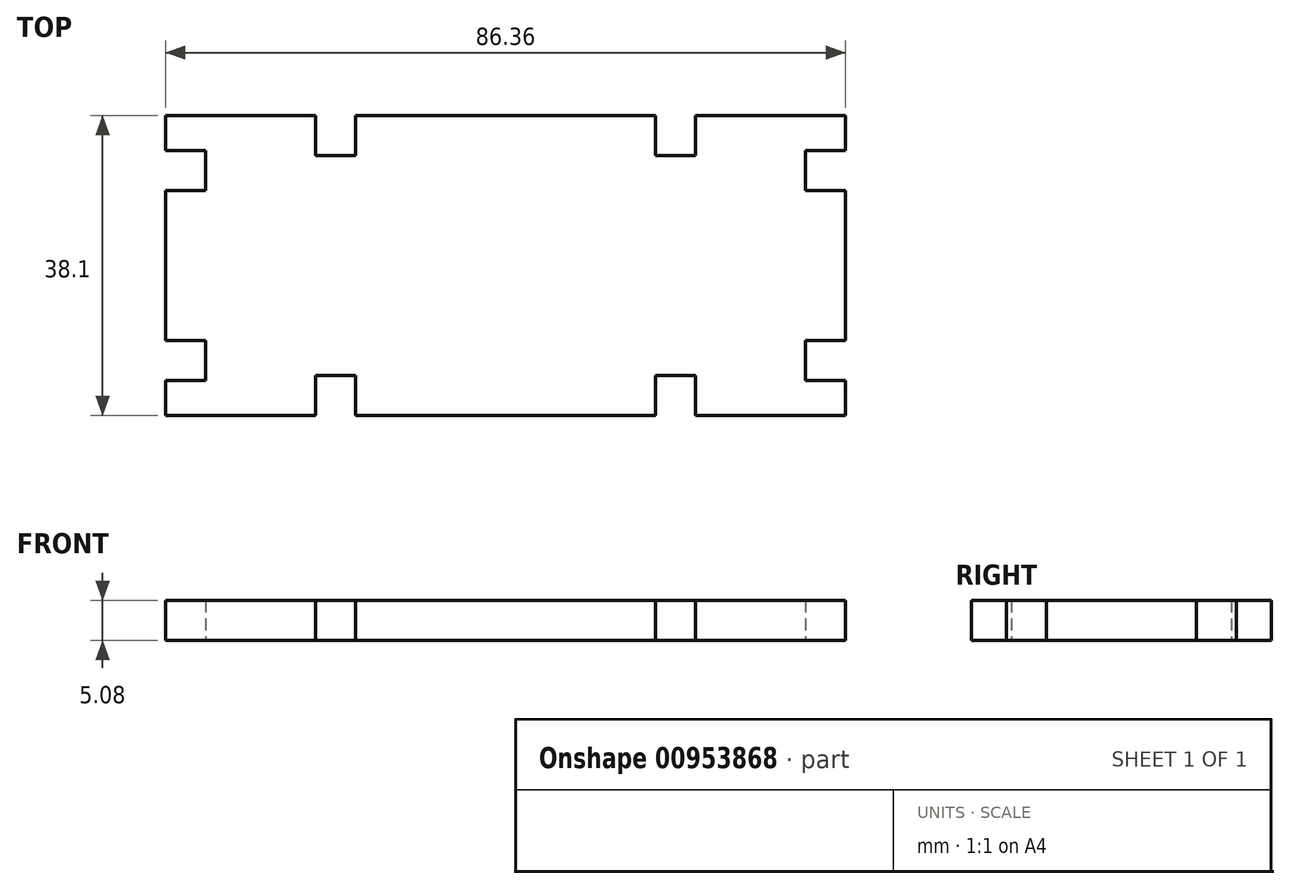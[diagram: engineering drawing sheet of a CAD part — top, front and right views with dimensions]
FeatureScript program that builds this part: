
annotation { "Feature Type Name" : "Feature", "Feature Type Description" : "" }
export const myFeature = defineFeature(function(context is Context, id is Id, definition is map)
    precondition{}
    {
        {
            var Q0;
            Q0=qCreatedBy(makeId("Top.planeOp"),FACE);
            var sketch = newSketch(context, id + "F0", { "sketchPlane" : qUnion([Q0])});
            skLineSegment(sketch, "E0.top", {"start": v(-43.18, -19.05) * mm, "end": v(43.18, -19.05) * mm});
            skLineSegment(sketch, "E0.right", {"start": v(43.18, 19.05) * mm, "end": v(43.18, -19.05) * mm});
            skPoint(sketch, "E0.middle", {"position": v(0, 0) * mm});
            skLineSegment(sketch, "E1", {"start": v(-43.18, 0) * mm, "end": v(43.18, 0) * mm});
            skLineSegment(sketch, "E2", {"start": v(-43.18, 19.05) * mm, "end": v(-43.18, 0) * mm});
            skLineSegment(sketch, "E3", {"start": v(-43.18, 0) * mm, "end": v(-43.18, -19.05) * mm});
            skLineSegment(sketch, "E4", {"start": v(0, 0) * mm, "end": v(0, 19.05) * mm});
            skLineSegment(sketch, "E5", {"start": v(-43.18, 19.05) * mm, "end": v(0, 19.05) * mm});
            skLineSegment(sketch, "E6", {"start": v(0, 19.05) * mm, "end": v(43.18, 19.05) * mm});
            skLineSegment(sketch, "E7", {"start": v(0, 19.05) * mm, "end": v(-38.1, 19.05) * mm});
            skLineSegment(sketch, "E8", {"start": v(0, 19.05) * mm, "end": v(38.1, 19.05) * mm});
            skLineSegment(sketch, "E9", {"start": v(-19.05, 19.05) * mm, "end": v(-19.05, 13.97) * mm});
            skLineSegment(sketch, "E10", {"start": v(-19.05, 13.97) * mm, "end": v(-24.13, 13.97) * mm});
            skLineSegment(sketch, "E11", {"start": v(-24.13, 13.97) * mm, "end": v(-24.13, 19.05) * mm});
            skLineSegment(sketch, "E12.MirrorCS", {"start": v(19.05, 19.05) * mm, "end": v(19.05, 13.97) * mm});
            skLineSegment(sketch, "E13.MirrorCS", {"start": v(19.05, 13.97) * mm, "end": v(24.13, 13.97) * mm});
            skLineSegment(sketch, "E14.MirrorCS", {"start": v(24.13, 13.97) * mm, "end": v(24.13, 19.05) * mm});
            skLineSegment(sketch, "E15.MirrorCS", {"start": v(-19.05, -13.97) * mm, "end": v(-24.13, -13.97) * mm});
            skLineSegment(sketch, "E16.MirrorCS", {"start": v(-24.13, -13.97) * mm, "end": v(-24.13, -19.05) * mm});
            skLineSegment(sketch, "E17.MirrorCS", {"start": v(-19.05, -19.05) * mm, "end": v(-19.05, -13.97) * mm});
            skLineSegment(sketch, "E18.MirrorCS", {"start": v(19.05, -13.97) * mm, "end": v(24.13, -13.97) * mm});
            skLineSegment(sketch, "E19.MirrorCS", {"start": v(19.05, -19.05) * mm, "end": v(19.05, -13.97) * mm});
            skLineSegment(sketch, "E20.MirrorCS", {"start": v(24.13, -13.97) * mm, "end": v(24.13, -19.05) * mm});
            skLineSegment(sketch, "E21.MirrorCS", {"start": v(-38.1, 14.6) * mm, "end": v(-43.18, 14.6) * mm});
            skLineSegment(sketch, "E22.MirrorCS", {"start": v(-38.1, 9.53) * mm, "end": v(-38.1, 14.6) * mm});
            skLineSegment(sketch, "E23.MirrorCS", {"start": v(-43.18, 9.53) * mm, "end": v(-38.1, 9.53) * mm});
            skLineSegment(sketch, "E24.MirrorCS", {"start": v(-38.1, -9.52) * mm, "end": v(-38.1, -14.6) * mm});
            skLineSegment(sketch, "E25.MirrorCS", {"start": v(-38.1, -14.6) * mm, "end": v(-43.18, -14.6) * mm});
            skLineSegment(sketch, "E26.MirrorCS", {"start": v(-43.18, -9.53) * mm, "end": v(-38.1, -9.52) * mm});
            skLineSegment(sketch, "E27.MirrorCS", {"start": v(38.1, 9.53) * mm, "end": v(38.1, 14.6) * mm});
            skLineSegment(sketch, "E28.MirrorCS", {"start": v(38.1, 14.6) * mm, "end": v(43.18, 14.6) * mm});
            skLineSegment(sketch, "E29.MirrorCS", {"start": v(43.18, 9.53) * mm, "end": v(38.1, 9.53) * mm});
            skLineSegment(sketch, "E30.MirrorCS", {"start": v(43.18, -9.52) * mm, "end": v(38.1, -9.52) * mm});
            skLineSegment(sketch, "E31.MirrorCS", {"start": v(38.1, -9.52) * mm, "end": v(38.1, -14.6) * mm});
            skLineSegment(sketch, "E32.MirrorCS", {"start": v(38.1, -14.6) * mm, "end": v(43.18, -14.6) * mm});
            skSolve(sketch);
        }
        {
            var Q0;
            {var subQ2=sQuery(id+"F0.wireOp",EDGE,"E4");Q0=makeQuery(id+"F0.imprint","IMPRINT",FACE,{"disambiguationData":[TD([[makeQuery(id+"F0.imprint","IMPRINT",EDGE,{"derivedFrom":subQ2}),1.0]])]});}
            var Q1;
            Q1=makeQuery(id+"F0.imprint","IMPRINT",FACE,{"disambiguationData":[TD([[makeQuery(id+"F0.imprint","IMPRINT",EDGE,{"derivedFrom":sQuery(id+"F0.wireOp",EDGE,"E15.MirrorCS")}),-1.0]])]});
            var Q2;
            {var subQ2=sQuery(id+"F0.wireOp",EDGE,"E4");Q2=makeQuery(id+"F0.imprint","IMPRINT",FACE,{"disambiguationData":[TD([[makeQuery(id+"F0.imprint","IMPRINT",EDGE,{"derivedFrom":subQ2}),-1.0]])]});}
            var Q3;
            {var subQ0=sQuery(id+"F0.wireOp",EDGE,"e83fc017-39d4-481e-bc65-dc40bb9258ac0.MirrorCS");Q3=makeQuery(id+"F0.imprint","IMPRINT",FACE,{"disambiguationData":[TD([[makeQuery(id+"F0.imprint","IMPRINT",EDGE,{"derivedFrom":subQ0}),1.0]])]});}
            var Q4;
            {var subQ0=sQuery(id+"F0.wireOp",EDGE,"SRaaNcdm-yG1X-ibsk-qxvO-wYVT8ddMniTX");Q4=makeQuery(id+"F0.imprint","IMPRINT",FACE,{"disambiguationData":[TD([[makeQuery(id+"F0.imprint","IMPRINT",EDGE,{"derivedFrom":subQ0}),-1.0]])]});}
            var Q5;
            {var subQ0=sQuery(id+"F0.wireOp",EDGE,"dc97ce03-7580-4040-bbae-75c83189a32a0.MirrorCS");Q5=makeQuery(id+"F0.imprint","IMPRINT",FACE,{"disambiguationData":[TD([[makeQuery(id+"F0.imprint","IMPRINT",EDGE,{"derivedFrom":subQ0}),1.0]])]});}
            var Q6;
            {var subQ0=sQuery(id+"F0.wireOp",EDGE,"9f2743af-e30f-4eb7-846a-43b69b414f220.MirrorCS");Q6=makeQuery(id+"F0.imprint","IMPRINT",FACE,{"disambiguationData":[TD([[makeQuery(id+"F0.imprint","IMPRINT",EDGE,{"derivedFrom":subQ0}),-1.0]])]});}
            extrude(context, id + "F1", {"entities" : qUnion([Q0, Q1, Q2, Q3, Q4, Q5, Q6]), "depth" : 5.08 * mm, "offsetDistance" : 25.4 * mm});
        }
    });
